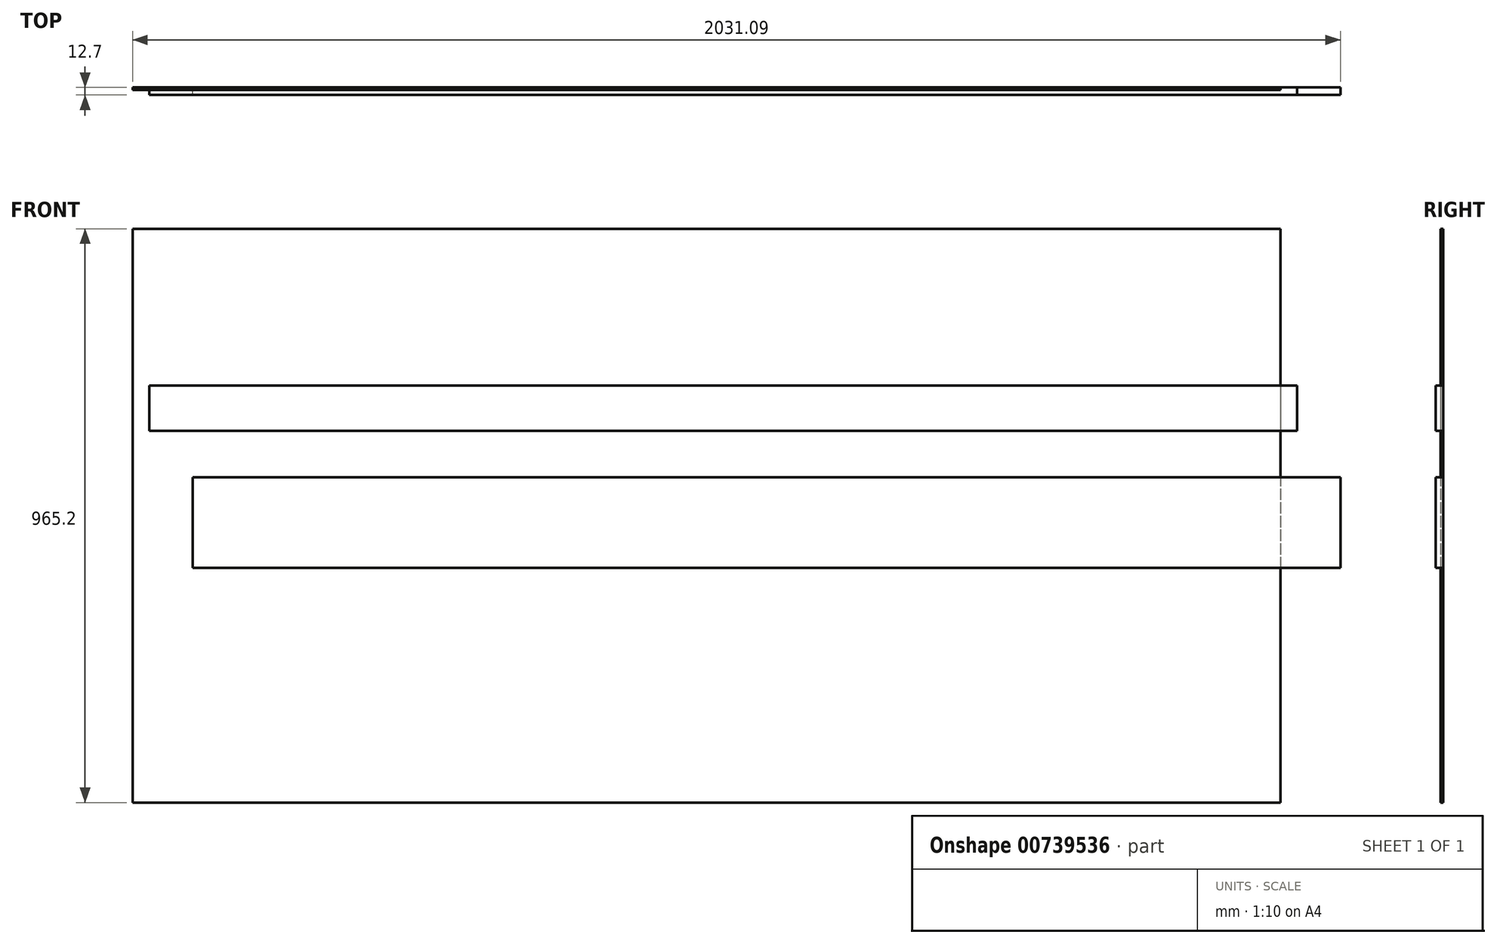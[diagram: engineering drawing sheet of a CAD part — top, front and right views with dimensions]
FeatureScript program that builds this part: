
annotation { "Feature Type Name" : "Feature", "Feature Type Description" : "" }
export const myFeature = defineFeature(function(context is Context, id is Id, definition is map)
    precondition{}
    {
        {
            var Q0;
            Q0=qCreatedBy(makeId("Front.planeOp"),FACE);
            var sketch = newSketch(context, id + "F0", { "sketchPlane" : qUnion([Q0])});
            skLineSegment(sketch, "E0.bottom", {"start": v(-864.51, 64.33) * mm, "end": v(1065.89, 64.33) * mm});
            skLineSegment(sketch, "E0.top", {"start": v(-864.51, -88.07) * mm, "end": v(1065.89, -88.07) * mm});
            skLineSegment(sketch, "E0.left", {"start": v(-864.51, 64.33) * mm, "end": v(-864.51, -88.07) * mm});
            skLineSegment(sketch, "E0.right", {"start": v(1065.89, 64.33) * mm, "end": v(1065.89, -88.07) * mm});
            skSolve(sketch);
        }
        {
            var Q0;
            Q0=makeQuery(id+"F0.imprint","IMPRINT",FACE,{"disambiguationData":[TD([[makeQuery(id+"F0.imprint","IMPRINT",EDGE,{"derivedFrom":sQuery(id+"F0.wireOp",EDGE,"E0.bottom")}),-1.0]])]});
            extrude(context, id + "F1", {"entities" : qUnion([Q0]), "depth" : 12.7 * mm, "offsetDistance" : 25.4 * mm});
        }
        {
            var Q0;
            Q0=qCreatedBy(makeId("Front.planeOp"),FACE);
            var sketch = newSketch(context, id + "F2", { "sketchPlane" : qUnion([Q0])});
            skLineSegment(sketch, "E1.bottom", {"start": v(-937.15, 142.83) * mm, "end": v(993.25, 142.83) * mm});
            skLineSegment(sketch, "E1.top", {"start": v(-937.15, 219.03) * mm, "end": v(993.25, 219.03) * mm});
            skLineSegment(sketch, "E1.left", {"start": v(-937.15, 142.83) * mm, "end": v(-937.15, 219.03) * mm});
            skLineSegment(sketch, "E1.right", {"start": v(993.25, 142.83) * mm, "end": v(993.25, 219.03) * mm});
            skPoint(sketch, "E1.middle", {"position": v(28.05, 180.93) * mm});
            skSolve(sketch);
        }
        {
            var Q0;
            Q0=makeQuery(id+"F2.imprint","IMPRINT",FACE,{"disambiguationData":[TD([[makeQuery(id+"F2.imprint","IMPRINT",EDGE,{"derivedFrom":sQuery(id+"F2.wireOp",EDGE,"E1.bottom")}),1.0]])]});
            extrude(context, id + "F3", {"entities" : qUnion([Q0]), "depth" : 12.7 * mm, "offsetDistance" : 25.4 * mm});
        }
        {
            var Q0;
            Q0=qCreatedBy(makeId("Front.planeOp"),FACE);
            var sketch = newSketch(context, id + "F4", { "sketchPlane" : qUnion([Q0])});
            skLineSegment(sketch, "E2.bottom", {"start": v(-965.2, 482.6) * mm, "end": v(965.2, 482.6) * mm});
            skLineSegment(sketch, "E2.top", {"start": v(-965.2, -482.6) * mm, "end": v(965.2, -482.6) * mm});
            skLineSegment(sketch, "E2.left", {"start": v(-965.2, 482.6) * mm, "end": v(-965.2, -482.6) * mm});
            skLineSegment(sketch, "E2.right", {"start": v(965.2, 482.6) * mm, "end": v(965.2, -482.6) * mm});
            skPoint(sketch, "E2.middle", {"position": v(0, 0) * mm});
            skSolve(sketch);
        }
        {
            var Q0;
            Q0=makeQuery(id+"F4.imprint","IMPRINT",FACE,{"disambiguationData":[TD([[makeQuery(id+"F4.imprint","IMPRINT",EDGE,{"derivedFrom":sQuery(id+"F4.wireOp",EDGE,"E2.bottom")}),-1.0]])]});
            extrude(context, id + "F5", {"entities" : qUnion([Q0]), "depth" : 4.06 * mm, "offsetDistance" : 25.4 * mm});
        }
    });
